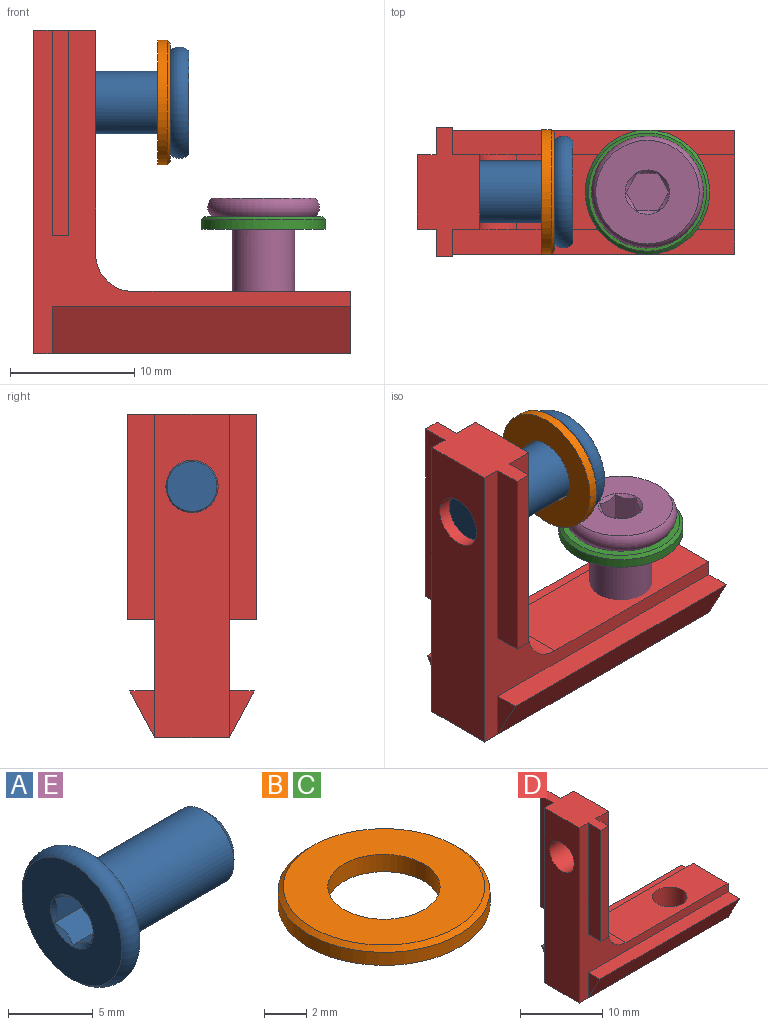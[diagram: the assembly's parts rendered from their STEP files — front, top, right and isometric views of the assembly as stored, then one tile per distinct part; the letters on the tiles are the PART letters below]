
ASSEMBLY  parts=5 mates=4
PART A: 14 faces, bbox 11.8x9.7x9.7 mm
  f0: cone r=1.78mm half-angle=45deg, axis (-1,0,0), area 3.1mm2, adj f5,f8,f9,f10,f11,f12,f13
  f1: torus R=3.5mm, axis (1,0,0), area 46.7mm2, adj f5,f6
  f2: cone r=2mm half-angle=45deg, axis (-1,0,0), area 10mm2, adj f3,f4
  f3: cylinder r=2.5mm len=9.5mm, axis (1,0,0), area 149.2mm2, adj f2,f6
  f4: plane 4x4mm, normal (1,0,0), area 12.6mm2, adj f2
  f5: plane 8.32x8.32mm, normal (-1,0,0), area 44.4mm2, adj f0,f1
  f6: plane 8.32x8.32mm, normal (1,0,0), area 34.8mm2, adj f1,f3
  f7: plane 3.46x3mm, normal (-1,0,0), area 7.8mm2, adj f8,f9,f10,f11,f12,f13
  f8: plane 2.25x1.5mm, normal (0,-0.5,-0.87), area 3.6mm2, adj f0,f7,f9,f13
  f9: plane 2.25x1.73mm, normal (0,-1,0), area 3.6mm2, adj f0,f7,f8,f10
  f10: plane 2.25x1.5mm, normal (0,-0.5,0.87), area 3.6mm2, adj f0,f7,f9,f11
  f11: plane 2.25x1.5mm, normal (0,0.5,0.87), area 3.6mm2, adj f0,f7,f10,f12
  f12: plane 2.25x1.73mm, normal (0,1,0), area 3.6mm2, adj f0,f7,f11,f13
  f13: plane 2.25x1.5mm, normal (0,0.5,-0.87), area 3.6mm2, adj f0,f7,f8,f12
PART B: 5 faces, bbox 10x10x1 mm
  f0: plane 9.5x9.5mm, normal (0,0,1), area 48.8mm2, adj f1,f4
  f1: cylinder r=2.65mm len=5.3mm, axis (0,0,-1), area 16.7mm2, adj f0,f2
  f2: plane 10x10mm, normal (0,0,-1), area 56.5mm2, adj f1,f3
  f3: cylinder r=5mm len=10mm, axis (0,0,-1), area 23.6mm2, adj f2,f4
  f4: cone r=5mm half-angle=45deg, axis (0,0,-1), area 10.8mm2, adj f0,f3
PART C: same geometry as B
PART D: 25 faces, bbox 25.5x10.4x26 mm
  f0: cylinder r=2.1mm len=5mm, axis (1,0,0), area 66mm2, adj f3,f8
  f1: cylinder r=2.1mm len=5mm, axis (0,0,1), area 66mm2, adj f4,f6
  f2: plane 10.4x5mm, normal (0,0,1), area 35.7mm2, adj f3,f8,f9,f10,f17,f19,f20,f21
  f3: plane 26x6mm, normal (-1,0,0), area 142.1mm2, adj f0,f2,f4,f9,f10
  f4: plane 25.5x6mm, normal (0,0,-1), area 139.1mm2, adj f1,f3,f5,f9,f10,f12,f16
  f5: plane 10x5mm, normal (1,0,0), area 37.5mm2, adj f4,f6,f9,f10,f12,f13,f14,f16
  f6: plane 17.5x6mm, normal (0,0,1), area 91.1mm2, adj f1,f5,f7,f9,f10
  f7: cylinder r=3mm len=6mm, axis (0,1,0), area 28.3mm2, adj f6,f8,f9,f10
  f8: plane 18x6mm, normal (1,0,0), area 94.1mm2, adj f0,f2,f7,f9,f10
  f9: plane 26x25.5mm, normal (0,-1,0), area 123mm2, adj f2,f3,f4,f5,f6,f7,f8,f14
  f10: plane 26x25.5mm, normal (0,1,0), area 123mm2, adj f2,f3,f4,f5,f6,f7,f8,f11
  f11: plane 3.75x2mm, normal (-1,0,0), area 3.8mm2, adj f10,f12,f13
  f12: plane 24x3.75mm, normal (0,0.88,-0.47), area 102mm2, adj f4,f5,f11,f13
  f13: plane 24x2mm, normal (0,0,1), area 48mm2, adj f5,f10,f11,f12
  f14: plane 24x2mm, normal (0,0,1), area 48mm2, adj f5,f9,f15,f16
  f15: plane 3.75x2mm, normal (-1,0,0), area 3.8mm2, adj f9,f14,f16
  f16: plane 24x3.75mm, normal (0,-0.88,-0.47), area 102mm2, adj f4,f5,f14,f15
  f17: plane 16.5x1.3mm, normal (0,1,0), area 21.4mm2, adj f2,f18,f19,f20
  f18: plane 2.2x1.3mm, normal (0,0,-1), area 2.9mm2, adj f10,f17,f19,f20
  f19: plane 16.5x2.2mm, normal (1,0,0), area 36.3mm2, adj f2,f10,f17,f18
  f20: plane 16.5x2.2mm, normal (-1,0,0), area 36.3mm2, adj f2,f10,f17,f18
  f21: plane 16.5x2.2mm, normal (-1,0,0), area 36.3mm2, adj f2,f9,f23,f24
  f22: plane 16.5x2.2mm, normal (1,0,0), area 36.3mm2, adj f2,f9,f23,f24
  f23: plane 2.2x1.3mm, normal (0,0,-1), area 2.9mm2, adj f9,f21,f22,f24
  f24: plane 16.5x1.3mm, normal (0,-1,0), area 21.4mm2, adj f2,f21,f22,f23
PART E: same geometry as A
PLACE A rot(axis=(0,1,0),180deg) t=(3,0,20.2)mm
PLACE B rot(axis=(0,1,0),90deg) t=(10.5,0,20.2)mm
PLACE C rot(axis=(0,0,1),180deg) t=(18.5,0,10.5)mm
PLACE D at identity fixed
PLACE E rot(axis=(0,1,0),90deg) t=(18.5,0,3)mm
MATE fastened E.f0 <-> C.f1  axis (0,0,-1) through (18.5,0,11)mm
MATE fastened B.f1 <-> D.f0  axis (1,0,0) through (10,0,20.2)mm
MATE fastened C.f1 <-> D.f1  axis (0,0,1) through (18.5,0,10)mm
MATE fastened A.f0 <-> B.f1  axis (-1,0,0) through (11,0,20.2)mm
